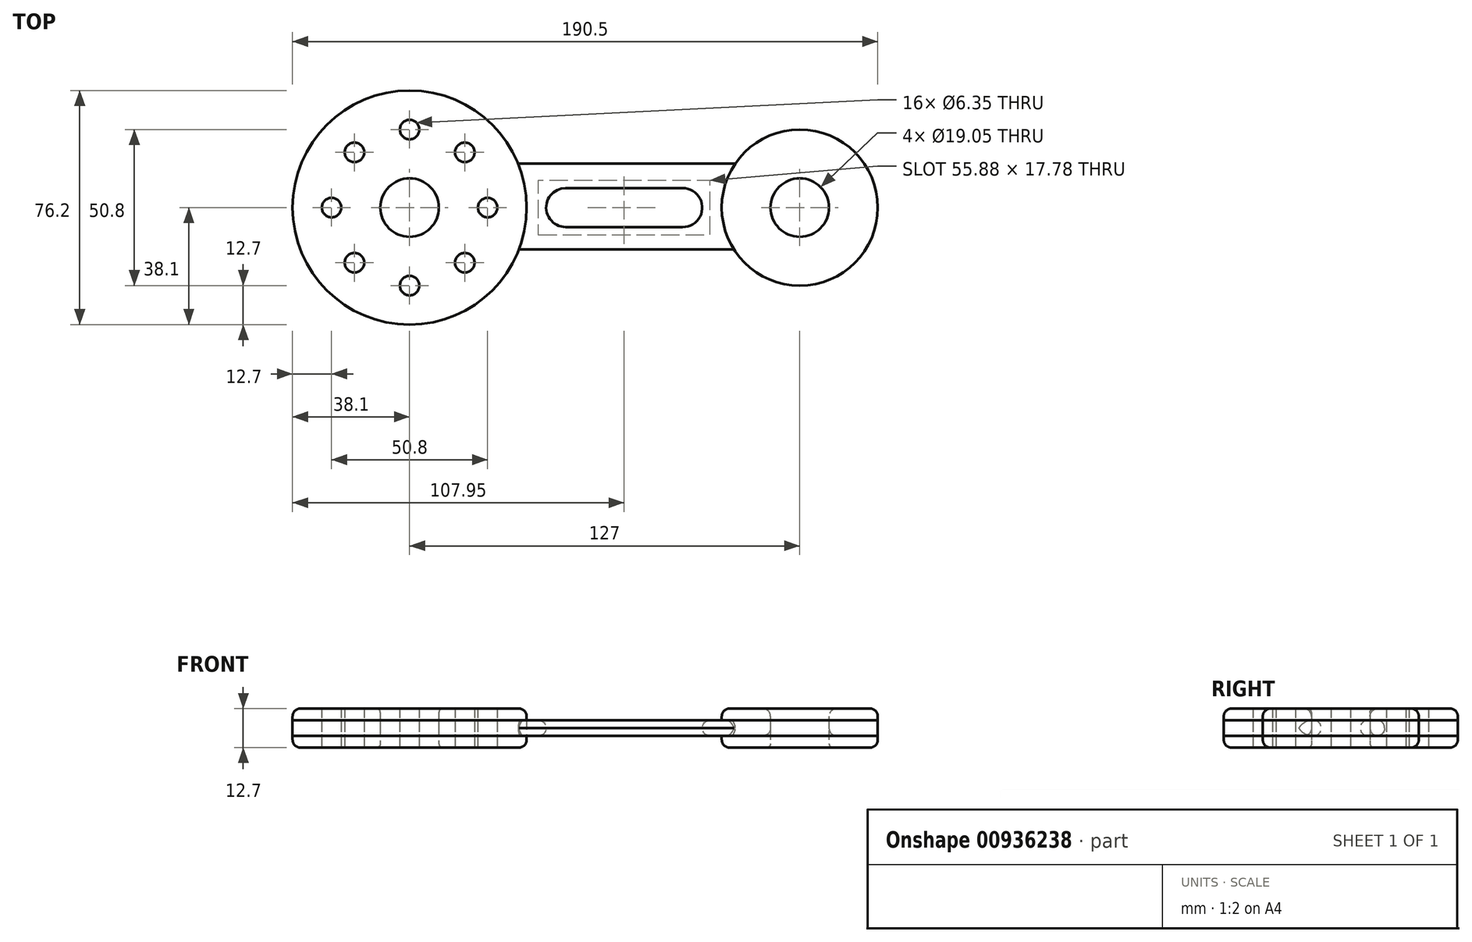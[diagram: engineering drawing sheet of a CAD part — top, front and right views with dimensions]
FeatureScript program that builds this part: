
annotation { "Feature Type Name" : "Feature", "Feature Type Description" : "" }
export const myFeature = defineFeature(function(context is Context, id is Id, definition is map)
    precondition{}
    {
        {
            var Q0;
            Q0=qCreatedBy(makeId("Top.planeOp"),FACE);
            var sketch = newSketch(context, id + "F0", { "sketchPlane" : qUnion([Q0])});
            skCircle(sketch, "E0", {"center": v(0, 0) * mm, "radius": 38.1 * mm});
            skCircle(sketch, "E1", {"center": v(127, 0) * mm, "radius": 25.4 * mm});
            skLineSegment(sketch, "E2", {"start": v(35.32, 14.29) * mm, "end": v(106, 14.29) * mm});
            skLineSegment(sketch, "E3", {"start": v(35.32, -14.29) * mm, "end": v(106, -14.29) * mm});
            skCircle(sketch, "E4", {"center": v(0, 0) * mm, "radius": 9.53 * mm});
            skCircle(sketch, "E5", {"center": v(127, 0) * mm, "radius": 9.53 * mm});
            skLineSegment(sketch, "E6", {"start": v(50.8, 0) * mm, "end": v(88.9, 0) * mm, "construction": true});
            skArc(sketch, "E7.0.startCap", {"start": v(50.8, -6.35) * mm, "mid": v(44.45, 0) * mm, "end": v(50.8, 6.35) * mm});
            skArc(sketch, "E7.0.endCap", {"start": v(88.9, 6.35) * mm, "mid": v(95.25, 0) * mm, "end": v(88.9, -6.35) * mm});
            skLineSegment(sketch, "E7.0.left", {"start": v(50.8, 6.35) * mm, "end": v(88.9, 6.35) * mm});
            skLineSegment(sketch, "E7.0.right", {"start": v(50.8, -6.35) * mm, "end": v(88.9, -6.35) * mm});
            skCircle(sketch, "E8", {"center": v(0, 0) * mm, "radius": 25.4 * mm, "construction": true});
            skCircle(sketch, "E9", {"center": v(0, 25.4) * mm, "radius": 3.18 * mm});
            skCircle(sketch, "E10.1.1", {"center": v(-17.96, 17.96) * mm, "radius": 3.18 * mm});
            skCircle(sketch, "E10.2.1", {"center": v(-25.4, 0) * mm, "radius": 3.18 * mm});
            skCircle(sketch, "E10.3.1", {"center": v(-17.96, -17.96) * mm, "radius": 3.18 * mm});
            skCircle(sketch, "E10.4.1", {"center": v(0, -25.4) * mm, "radius": 3.18 * mm});
            skCircle(sketch, "E10.5.1", {"center": v(17.96, -17.96) * mm, "radius": 3.18 * mm});
            skCircle(sketch, "E10.6.1", {"center": v(25.4, 0) * mm, "radius": 3.18 * mm});
            skCircle(sketch, "E10.7.1", {"center": v(17.96, 17.96) * mm, "radius": 3.18 * mm});
            skSolve(sketch);
        }
        {
            var Q0;
            Q0=makeQuery(id+"F0.imprint","IMPRINT",FACE,{"disambiguationData":[TD([[makeQuery(id+"F0.imprint","IMPRINT",EDGE,{"derivedFrom":sQuery(id+"F0.wireOp",EDGE,"E4")}),-1.0]])]});
            var Q1;
            Q1=makeQuery(id+"F0.imprint","IMPRINT",FACE,{"disambiguationData":[TD([[makeQuery(id+"F0.imprint","IMPRINT",EDGE,{"derivedFrom":sQuery(id+"F0.wireOp",EDGE,"E5")}),-1.0]])]});
            extrude(context, id + "F1", {"entities" : qUnion([Q0, Q1]), "endBound" : BoundingType.SYMMETRIC, "depth" : 12.7 * mm, "offsetDistance" : 25.4 * mm});
        }
        {
            var Q0;
            Q0 = qSketchRegion(id + "F0", true);
            extrude(context, id + "F2", {"entities" : qUnion([Q0]), "endBound" : BoundingType.SYMMETRIC, "depth" : 5.08 * mm, "offsetDistance" : 25.4 * mm});
        }
        {
            var Q0;
            Q0=makeQuery(id+"F1.opExtrude","CAP_EDGE",EDGE,{"disambiguationData":[OSD([sQuery(id+"F0.wireOp",EDGE,"E0")])],"isStart":false});
            var Q1;
            Q1=makeQuery(id+"F1.opExtrude","CAP_EDGE",EDGE,{"disambiguationData":[OSD([sQuery(id+"F0.wireOp",EDGE,"E1")])],"isStart":false});
            var Q2;
            Q2=makeQuery(id+"F1.opExtrude","CAP_EDGE",EDGE,{"disambiguationData":[OSD([sQuery(id+"F0.wireOp",EDGE,"E0")])],"isStart":true});
            var Q3;
            Q3=makeQuery(id+"F1.opExtrude","CAP_EDGE",EDGE,{"disambiguationData":[OSD([sQuery(id+"F0.wireOp",EDGE,"E1")])],"isStart":true});
            fillet(context, id + "F3", {"entities" : qUnion([Q0, Q1, Q2, Q3]), "radius" : 2.54 * mm, "tangentPropagation" : true, "allowEdgeOverflow" : false});
        }
        {
            var Q0;
            Q0=makeQuery(id+"F2.opExtrude","CAP_EDGE",EDGE,{"disambiguationData":[OSD([sQuery(id+"F0.wireOp",EDGE,"E2")])],"isStart":false});
            var Q1;
            Q1=makeQuery(id+"F2.opExtrude","CAP_EDGE",EDGE,{"disambiguationData":[OSD([sQuery(id+"F0.wireOp",EDGE,"E2")])],"isStart":true});
            var Q2;
            Q2=makeQuery(id+"F2.opExtrude","CAP_EDGE",EDGE,{"disambiguationData":[OSD([sQuery(id+"F0.wireOp",EDGE,"E7.0.left")])],"isStart":false});
            var Q3;
            Q3=makeQuery(id+"F2.opExtrude","CAP_EDGE",EDGE,{"disambiguationData":[OSD([sQuery(id+"F0.wireOp",EDGE,"E7.0.right")])],"isStart":false});
            var Q4;
            Q4=makeQuery(id+"F1.opExtrude","CAP_EDGE",EDGE,{"disambiguationData":[OSD([sQuery(id+"F0.wireOp",EDGE,"E5")])],"isStart":false});
            var Q5;
            Q5=makeQuery(id+"F2.opExtrude","CAP_EDGE",EDGE,{"disambiguationData":[OSD([sQuery(id+"F0.wireOp",EDGE,"E5")])],"isStart":true});
            var Q6;
            Q6=makeQuery(id+"F2.opExtrude","CAP_EDGE",EDGE,{"disambiguationData":[OSD([sQuery(id+"F0.wireOp",EDGE,"E7.0.right")])],"isStart":true});
            fillet(context, id + "F4", {"entities" : qUnion([Q0, Q1, Q2, Q3, Q4, Q5, Q6]), "radius" : 2.54 * mm, "tangentPropagation" : true, "allowEdgeOverflow" : false});
        }
        {
            var Q0;
            Q0=makeQuery(id+"F2.opExtrude","CAP_EDGE",EDGE,{"disambiguationData":[OSD([sQuery(id+"F0.wireOp",EDGE,"E3")])],"isStart":false});
            var Q1;
            Q1=makeQuery(id+"F2.opExtrude","CAP_EDGE",EDGE,{"disambiguationData":[OSD([sQuery(id+"F0.wireOp",EDGE,"E3")])],"isStart":true});
            fillet(context, id + "F5", {"entities" : qUnion([Q0, Q1]), "radius" : 5.08 * mm, "tangentPropagation" : true, "allowEdgeOverflow" : false});
        }
        {
            var Q0;
            Q0=makeQuery(id+"F1.opExtrude","CAP_EDGE",EDGE,{"disambiguationData":[OSD([sQuery(id+"F0.wireOp",EDGE,"E4")])],"isStart":false});
            var Q1;
            Q1=makeQuery(id+"F1.opExtrude","CAP_EDGE",EDGE,{"disambiguationData":[OSD([sQuery(id+"F0.wireOp",EDGE,"E4")])],"isStart":true});
            var Q2;
            Q2=makeQuery(id+"F1.opExtrude","CAP_EDGE",EDGE,{"disambiguationData":[OSD([sQuery(id+"F0.wireOp",EDGE,"E5")])],"isStart":true});
            fillet(context, id + "F6", {"entities" : qUnion([Q0, Q1, Q2]), "radius" : 1.27 * mm, "tangentPropagation" : true, "allowEdgeOverflow" : false});
        }
    });
